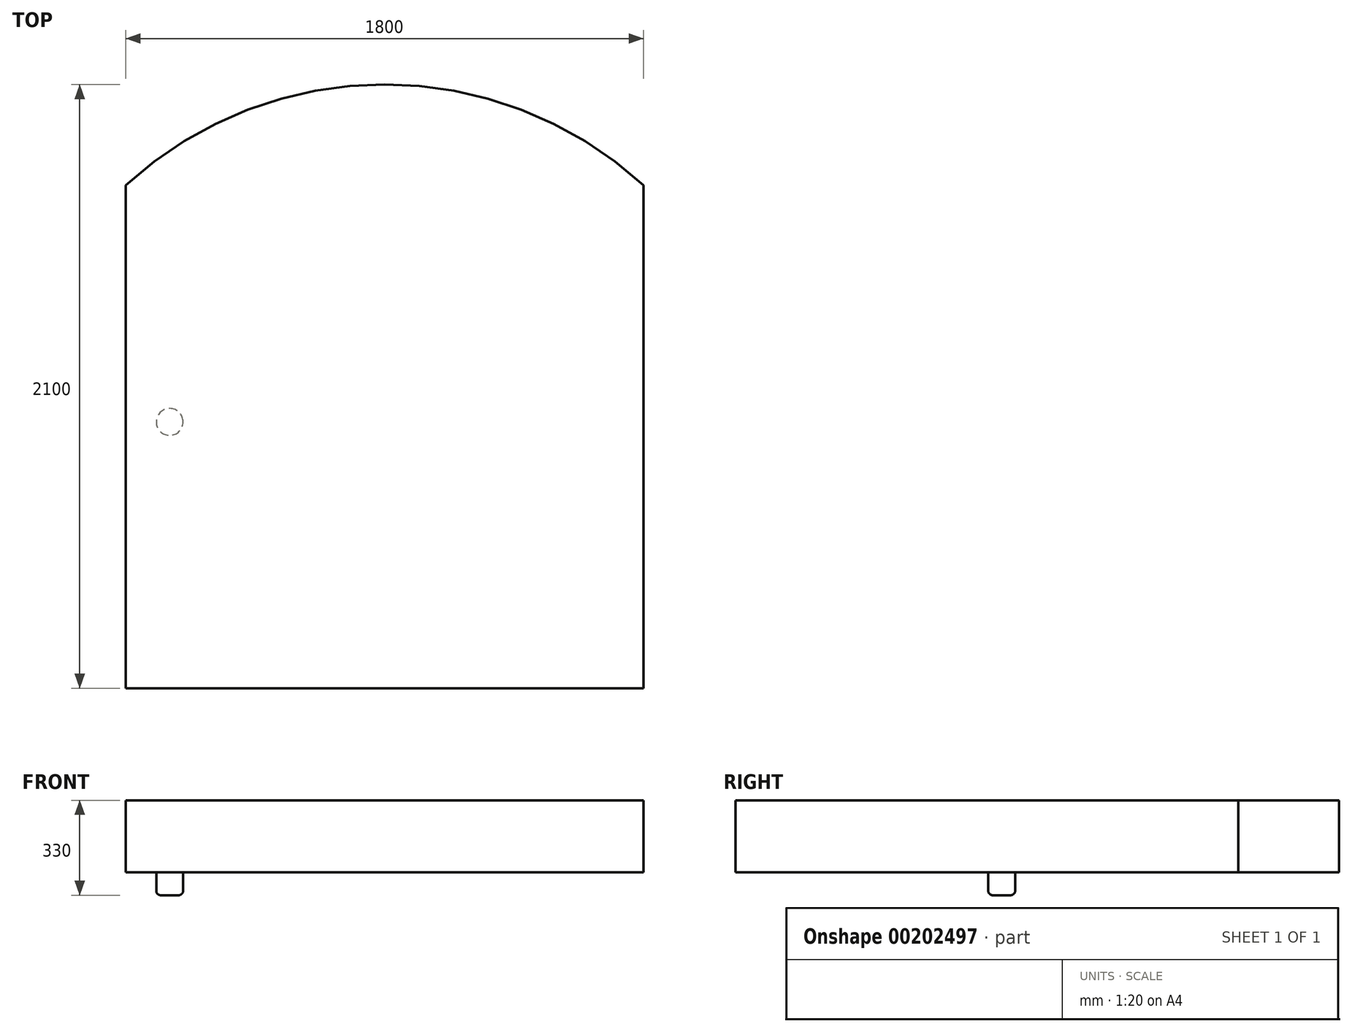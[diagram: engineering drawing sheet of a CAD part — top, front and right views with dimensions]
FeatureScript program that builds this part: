
annotation { "Feature Type Name" : "Feature", "Feature Type Description" : "" }
export const myFeature = defineFeature(function(context is Context, id is Id, definition is map)
    precondition{}
    {
        {
            var Q0;
            Q0=qCreatedBy(makeId("Top.planeOp"),FACE);
            var sketch = newSketch(context, id + "F0", { "sketchPlane" : qUnion([Q0])});
            skLineSegment(sketch, "E0.top", {"start": v(900, -875) * mm, "end": v(-900, -875) * mm});
            skLineSegment(sketch, "E0.left", {"start": v(900, 875) * mm, "end": v(900, -875) * mm});
            skLineSegment(sketch, "E0.right", {"start": v(-900, 875) * mm, "end": v(-900, -875) * mm});
            skPoint(sketch, "E0.middle", {"position": v(0, 0) * mm});
            skArc(sketch, "E1", {"start": v(900, 875) * mm, "mid": v(0, 1225) * mm, "end": v(-900, 875) * mm});
            skSolve(sketch);
        }
        {
            var Q0;
            Q0=makeQuery(id+"F0.imprint","IMPRINT",FACE,{"disambiguationData":[TD([[makeQuery(id+"F0.imprint","IMPRINT",EDGE,{"derivedFrom":sQuery(id+"F0.wireOp",EDGE,"E0.top")}),-1.0]])]});
            extrude(context, id + "F1", {"entities" : qUnion([Q0]), "endBound" : BoundingType.SYMMETRIC, "depth" : 250 * mm});
        }
        {
            var Q0;
            Q0=makeQuery(id+"F1.opExtrude","CAP_FACE",FACE,{"disambiguationData":[OSD([sQuery(id+"F0.wireOp",EDGE,"E0.top"),sQuery(id+"F0.wireOp",EDGE,"E0.left"),sQuery(id+"F0.wireOp",EDGE,"E0.right"),sQuery(id+"F0.wireOp",EDGE,"E1")])],"isStart":true});
            var sketch = newSketch(context, id + "F2", { "sketchPlane" : qUnion([Q0])});
            skCircle(sketch, "E2", {"center": v(-747.43, -51.44) * mm, "radius": 46.68 * mm});
            skSolve(sketch);
        }
        {
            var Q0;
            Q0=makeQuery(id+"F2.imprint","IMPRINT",FACE,{"disambiguationData":[TD([[makeQuery(id+"F2.imprint","IMPRINT",EDGE,{"derivedFrom":sQuery(id+"F2.wireOp",EDGE,"E2")}),1.0]])]});
            extrude(context, id + "F3", {"entities" : qUnion([Q0]), "operationType" : NewBodyOperationType.ADD, "depth" : 80 * mm});
        }
        {
            var Q0;
            Q0=makeQuery(id+"F3.opExtrude","CAP_EDGE",EDGE,{"disambiguationData":[OSD([sQuery(id+"F2.wireOp",EDGE,"E2")])],"isStart":false});
            fillet(context, id + "F4", {"entities" : qUnion([Q0]), "radius" : 15 * mm, "tangentPropagation" : true, "allowEdgeOverflow" : false});
        }
    });
